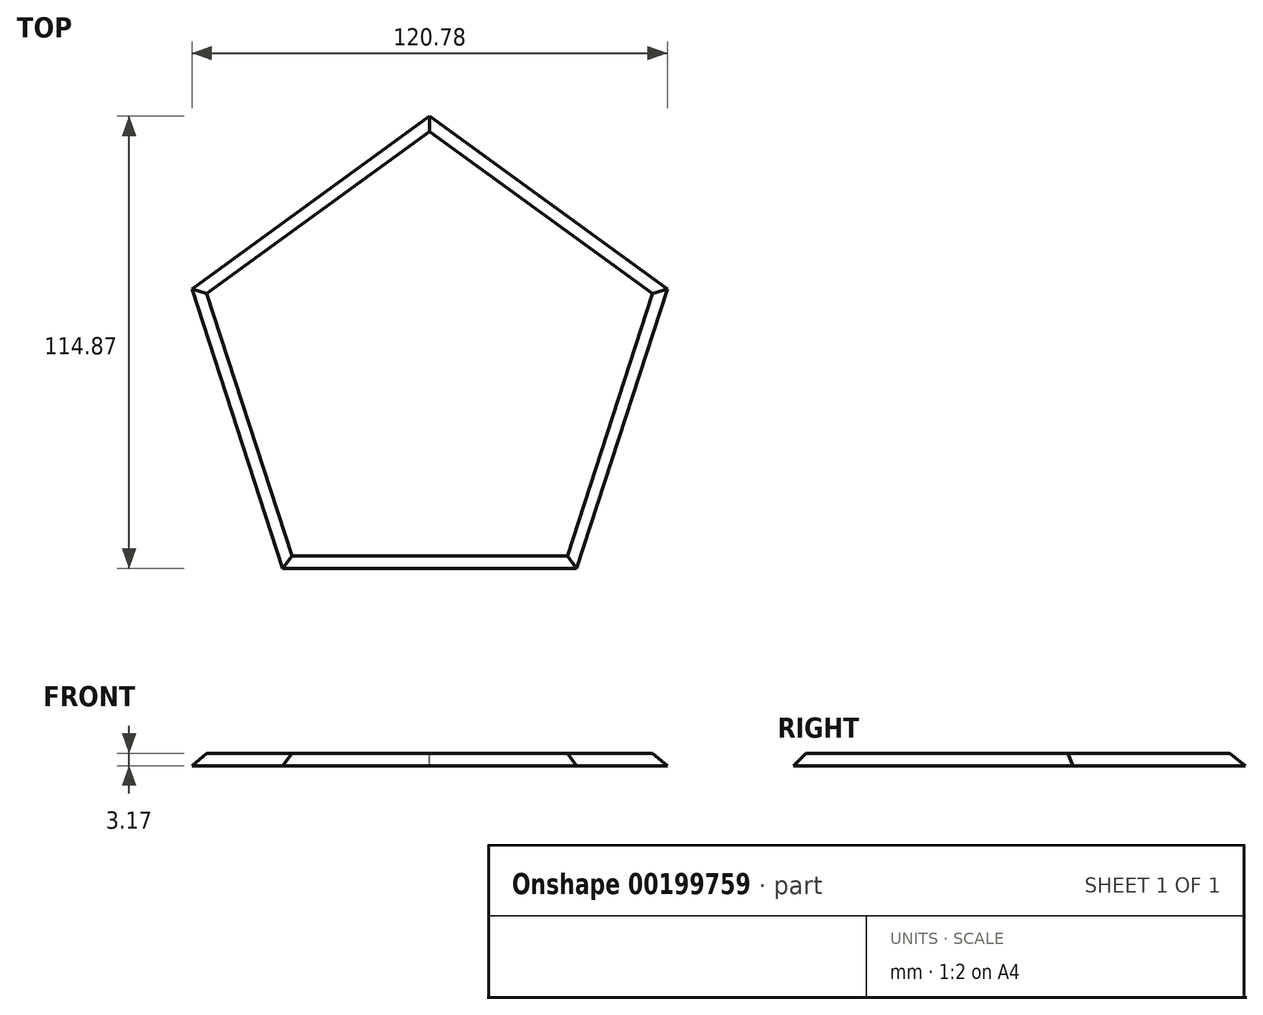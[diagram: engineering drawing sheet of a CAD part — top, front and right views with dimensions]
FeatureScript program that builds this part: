
annotation { "Feature Type Name" : "Feature", "Feature Type Description" : "" }
export const myFeature = defineFeature(function(context is Context, id is Id, definition is map)
    precondition{}
    {
        {
            var Q0;
            Q0=qCreatedBy(makeId("Top.planeOp"),FACE);
            var sketch = newSketch(context, id + "F0", { "sketchPlane" : qUnion([Q0])});
            skCircle(sketch, "E0.cCircle", {"center": v(0, 0) * mm, "radius": 63.5 * mm, "construction": true});
            skLineSegment(sketch, "E0.0", {"start": v(0, 63.5) * mm, "end": v(60.4, 19.62) * mm});
            skLineSegment(sketch, "E0.1", {"start": v(60.4, 19.62) * mm, "end": v(37.32, -51.37) * mm});
            skLineSegment(sketch, "E0.2", {"start": v(37.32, -51.37) * mm, "end": v(-37.32, -51.37) * mm});
            skLineSegment(sketch, "E0.3", {"start": v(-37.32, -51.37) * mm, "end": v(-60.4, 19.62) * mm});
            skLineSegment(sketch, "E0.4", {"start": v(-60.4, 19.62) * mm, "end": v(0, 63.5) * mm});
            skSolve(sketch);
        }
        {
            var Q0;
            Q0 = qSketchRegion(id + "F0", true);
            extrude(context, id + "F1", {"entities" : qUnion([Q0]), "depth" : 3.17 * mm});
        }
        {
            var Q0;
            Q0=makeQuery(id+"F1.opExtrude","CAP_FACE",FACE,{"disambiguationData":[OSD([sQuery(id+"F0.wireOp",EDGE,"E0.0"),sQuery(id+"F0.wireOp",EDGE,"E0.1"),sQuery(id+"F0.wireOp",EDGE,"E0.2"),sQuery(id+"F0.wireOp",EDGE,"E0.3"),sQuery(id+"F0.wireOp",EDGE,"E0.4")])],"isStart":false});
            chamfer(context, id + "F2", {"entities" : qUnion([Q0]), "width" : 3.17 * mm, "tangentPropagation" : true});
        }
    });
